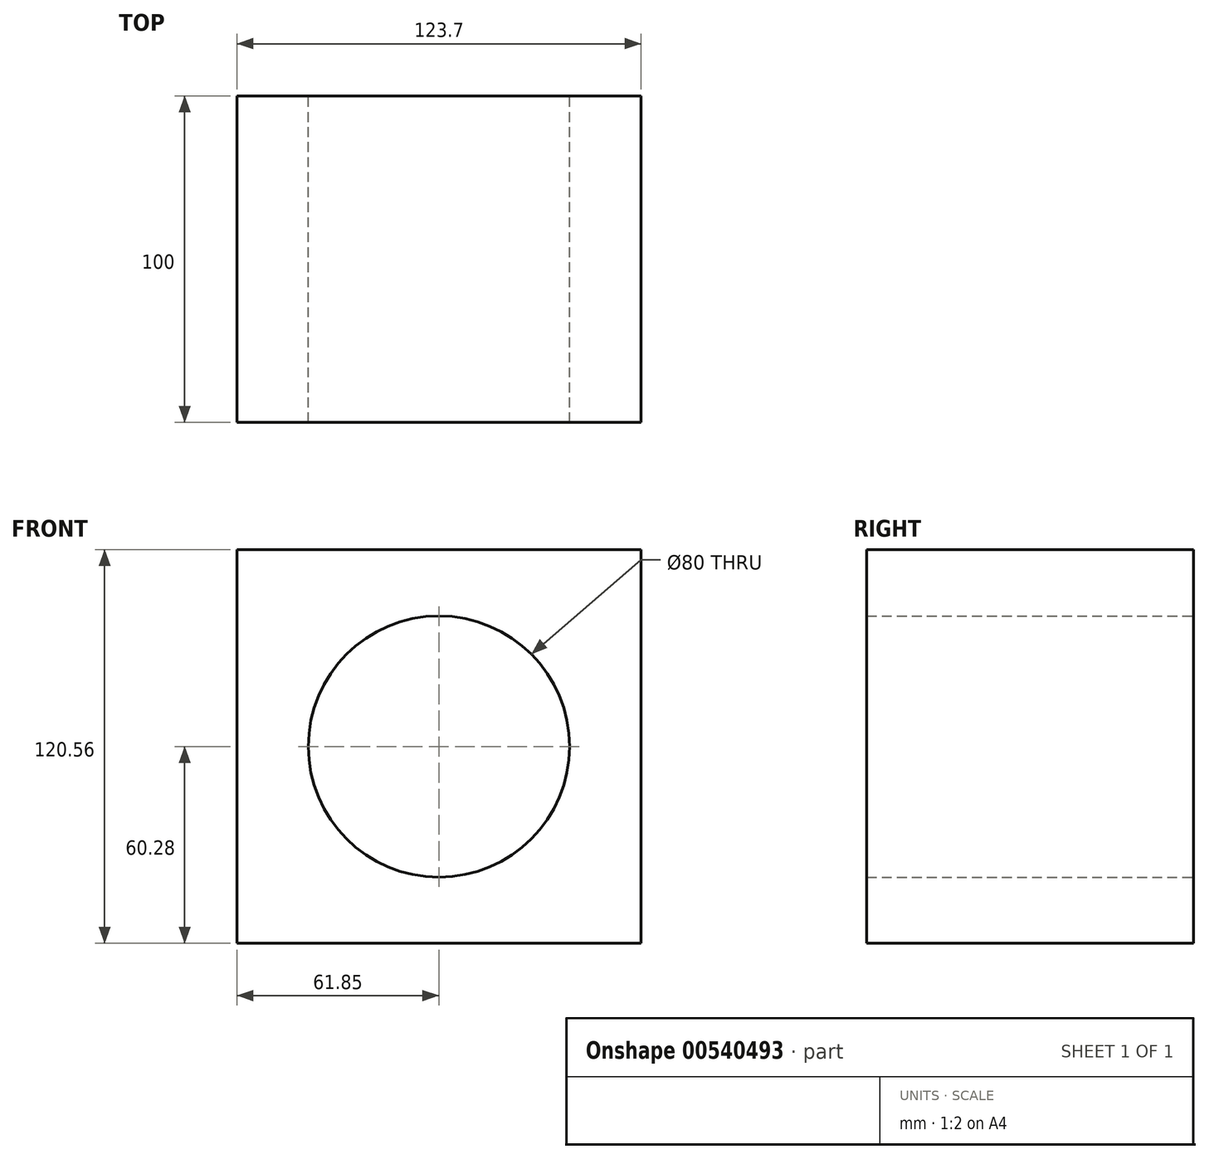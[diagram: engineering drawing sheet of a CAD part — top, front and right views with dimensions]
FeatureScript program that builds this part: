
annotation { "Feature Type Name" : "Feature", "Feature Type Description" : "" }
export const myFeature = defineFeature(function(context is Context, id is Id, definition is map)
    precondition{}
    {
        {
            var Q0;
            Q0=qCreatedBy(makeId("Front.planeOp"),FACE);
            var sketch = newSketch(context, id + "F0", { "sketchPlane" : qUnion([Q0])});
            skLineSegment(sketch, "E0.bottom", {"start": v(61.85, -60.28) * mm, "end": v(-61.85, -60.28) * mm});
            skLineSegment(sketch, "E0.top", {"start": v(61.85, 60.28) * mm, "end": v(-61.85, 60.28) * mm});
            skLineSegment(sketch, "E0.left", {"start": v(61.85, -60.28) * mm, "end": v(61.85, 60.28) * mm});
            skLineSegment(sketch, "E0.right", {"start": v(-61.85, -60.28) * mm, "end": v(-61.85, 60.28) * mm});
            skPoint(sketch, "E0.middle", {"position": v(0, 0) * mm});
            skSolve(sketch);
        }
        {
            var Q0;
            Q0=qCreatedBy(makeId("Front.planeOp"),FACE);
            var sketch = newSketch(context, id + "F1", { "sketchPlane" : qUnion([Q0])});
            skLineSegment(sketch, "E1.bottom", {"start": v(38.57, -34.77) * mm, "end": v(-38.57, -34.77) * mm});
            skLineSegment(sketch, "E1.top", {"start": v(38.57, 34.77) * mm, "end": v(-38.57, 34.77) * mm});
            skLineSegment(sketch, "E1.left", {"start": v(38.57, -34.77) * mm, "end": v(38.57, 34.77) * mm});
            skLineSegment(sketch, "E1.right", {"start": v(-38.57, -34.77) * mm, "end": v(-38.57, 34.77) * mm});
            skPoint(sketch, "E1.middle", {"position": v(0, 0) * mm});
            skSolve(sketch);
        }
        {
            var Q0;
            Q0=makeQuery(id+"F0.imprint","IMPRINT",FACE,{"disambiguationData":[TD([[makeQuery(id+"F0.imprint","IMPRINT",EDGE,{"derivedFrom":sQuery(id+"F0.wireOp",EDGE,"E0.bottom")}),-1.0]])]});
            extrude(context, id + "F2", {"entities" : qUnion([Q0]), "depth" : 100 * mm, "offsetDistance" : 25 * mm});
        }
        {
            var Q0;
            Q0=sQuery(id+"F1.wireOp",VERTEX,"E1.middle");
            var Q1;
            Q1=makeQuery(id+"F2.opExtrude","SWEPT_BODY",BODY,{"disambiguationData":[OSD([sQuery(id+"F0.wireOp",EDGE,"E0.bottom"),sQuery(id+"F0.wireOp",EDGE,"E0.top"),sQuery(id+"F0.wireOp",EDGE,"E0.left"),sQuery(id+"F0.wireOp",EDGE,"E0.right")])]});
            hole(context, id + "F3", {"style" : HoleStyle.SIMPLE, "endStyle" : HoleEndStyle.THROUGH, "oppositeDirection" : true, "holeDiameter" : 80 * mm, "isTappedThrough" : true, "tappedDepth" : 12 * mm, "tapClearance" : 3, "locations" : qUnion([Q0]), "scope" : qUnion([Q1])});
        }
    });
